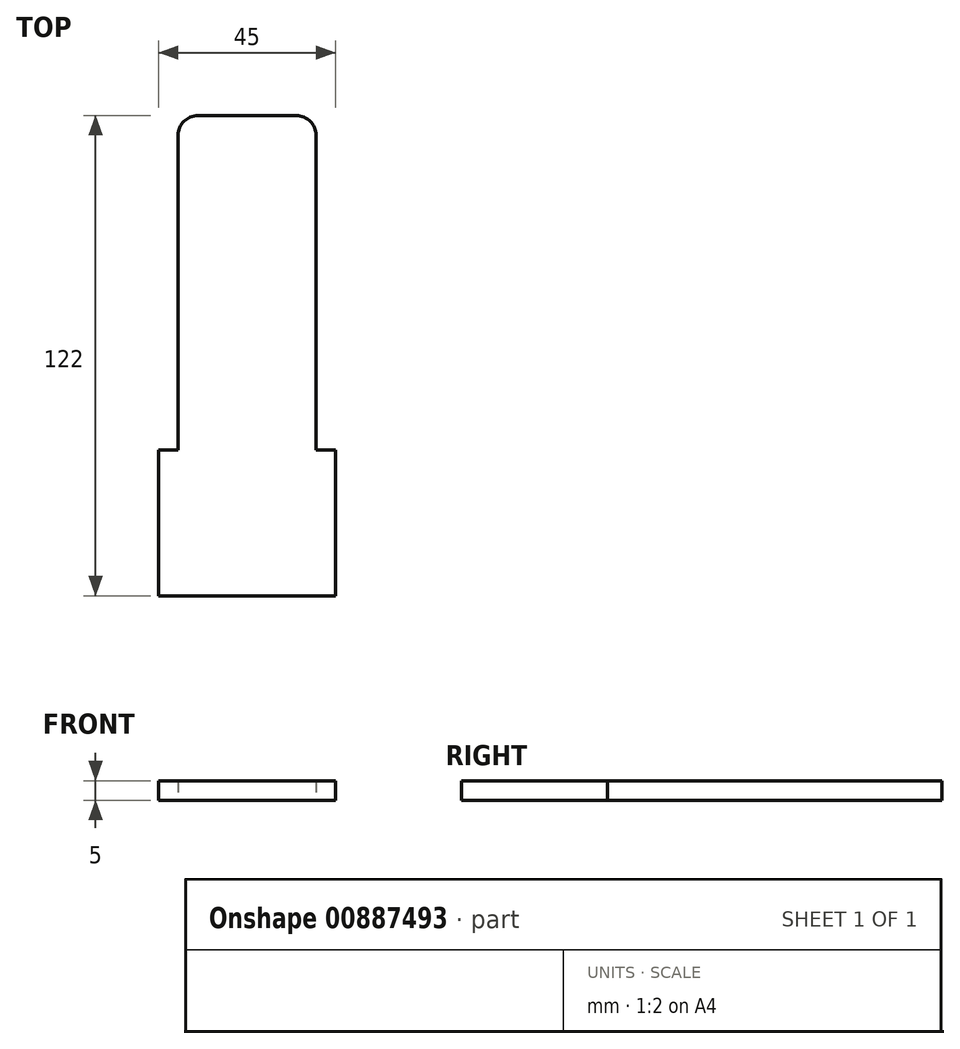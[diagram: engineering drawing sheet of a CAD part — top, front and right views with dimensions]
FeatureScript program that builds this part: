
annotation { "Feature Type Name" : "Feature", "Feature Type Description" : "" }
export const myFeature = defineFeature(function(context is Context, id is Id, definition is map)
    precondition{}
    {
        {
            var Q0;
            Q0=qCreatedBy(makeId("Top.planeOp"),FACE);
            var sketch = newSketch(context, id + "F0", { "sketchPlane" : qUnion([Q0])});
            skLineSegment(sketch, "E0.bottom", {"start": v(-17.5, 42.5) * mm, "end": v(17.5, 42.5) * mm});
            skLineSegment(sketch, "E0.left", {"start": v(-17.5, 42.5) * mm, "end": v(-17.5, -42.5) * mm});
            skLineSegment(sketch, "E0.right", {"start": v(17.5, 42.5) * mm, "end": v(17.5, -42.5) * mm});
            skLineSegment(sketch, "E1.top", {"start": v(-22.5, -79.5) * mm, "end": v(22.5, -79.5) * mm});
            skLineSegment(sketch, "E1.left", {"start": v(-22.5, -42.5) * mm, "end": v(-22.5, -79.5) * mm});
            skLineSegment(sketch, "E1.right", {"start": v(22.5, -42.5) * mm, "end": v(22.5, -79.5) * mm});
            skLineSegment(sketch, "E2", {"start": v(-17.5, 42.5) * mm, "end": v(17.5, -42.5) * mm, "construction": true});
            skLineSegment(sketch, "E3", {"start": v(-22.5, -42.5) * mm, "end": v(-17.5, -42.5) * mm});
            skLineSegment(sketch, "E4", {"start": v(22.5, -42.5) * mm, "end": v(17.5, -42.5) * mm});
            skSolve(sketch);
        }
        {
            var Q0;
            Q0=makeQuery(id+"F0.imprint","IMPRINT",FACE,{"disambiguationData":[TD([[makeQuery(id+"F0.imprint","IMPRINT",EDGE,{"derivedFrom":sQuery(id+"F0.wireOp",EDGE,"E0.bottom")}),-1.0]])]});
            extrude(context, id + "F1", {"entities" : qUnion([Q0]), "depth" : 5 * mm, "offsetDistance" : 25 * mm});
        }
        {
            var Q0;
            Q0=makeQuery(id+"F1.opExtrude","SWEPT_EDGE",EDGE,{"disambiguationData":[OSD([sQuery(id+"F0.wireOp",EDGE,"E0.bottom"),sQuery(id+"F0.wireOp",EDGE,"E0.right")])]});
            var Q1;
            Q1=makeQuery(id+"F1.opExtrude","SWEPT_EDGE",EDGE,{"disambiguationData":[OSD([sQuery(id+"F0.wireOp",EDGE,"E0.bottom"),sQuery(id+"F0.wireOp",EDGE,"E0.left")])]});
            fillet(context, id + "F2", {"entities" : qUnion([Q0, Q1]), "radius" : 5 * mm, "tangentPropagation" : true, "allowEdgeOverflow" : false});
        }
    });
